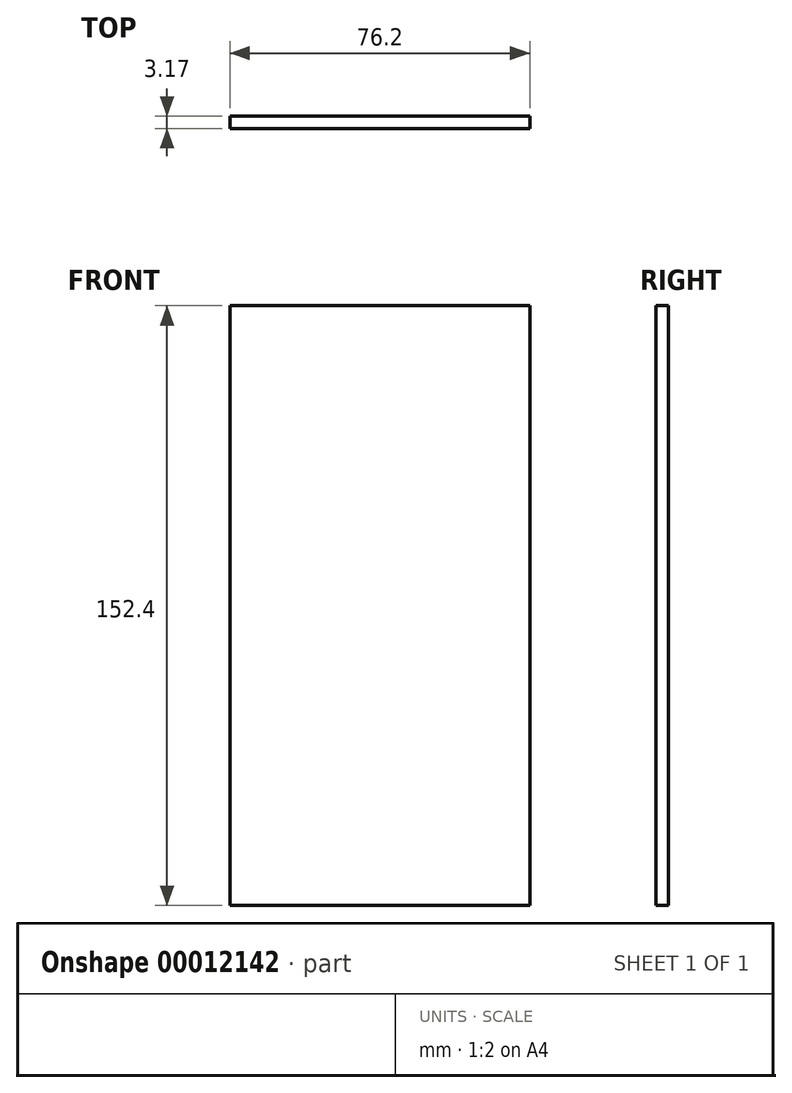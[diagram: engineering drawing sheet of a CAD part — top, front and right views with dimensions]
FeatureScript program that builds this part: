
annotation { "Feature Type Name" : "Feature", "Feature Type Description" : "" }
export const myFeature = defineFeature(function(context is Context, id is Id, definition is map)
    precondition{}
    {
        {
            var Q0;
            Q0=qCreatedBy(makeId("Front.planeOp"),FACE);
            var sketch = newSketch(context, id + "F0", { "sketchPlane" : qUnion([Q0])});
            skLineSegment(sketch, "E0.bottom", {"start": v(0, 0) * mm, "end": v(76.2, 0) * mm});
            skLineSegment(sketch, "E0.top", {"start": v(0, 152.4) * mm, "end": v(76.2, 152.4) * mm});
            skLineSegment(sketch, "E0.left", {"start": v(0, 0) * mm, "end": v(0, 152.4) * mm});
            skLineSegment(sketch, "E0.right", {"start": v(76.2, 0) * mm, "end": v(76.2, 152.4) * mm});
            skSolve(sketch);
        }
        {
            var Q0;
            Q0=makeQuery(id+"F0.imprint","IMPRINT",FACE,{"disambiguationData":[TD([[makeQuery(id+"F0.imprint","IMPRINT",EDGE,{"derivedFrom":sQuery(id+"F0.wireOp",EDGE,"E0.bottom")}),1.0]])]});
            extrude(context, id + "F1", {"entities" : qUnion([Q0]), "depth" : 3.17 * mm});
        }
    });
